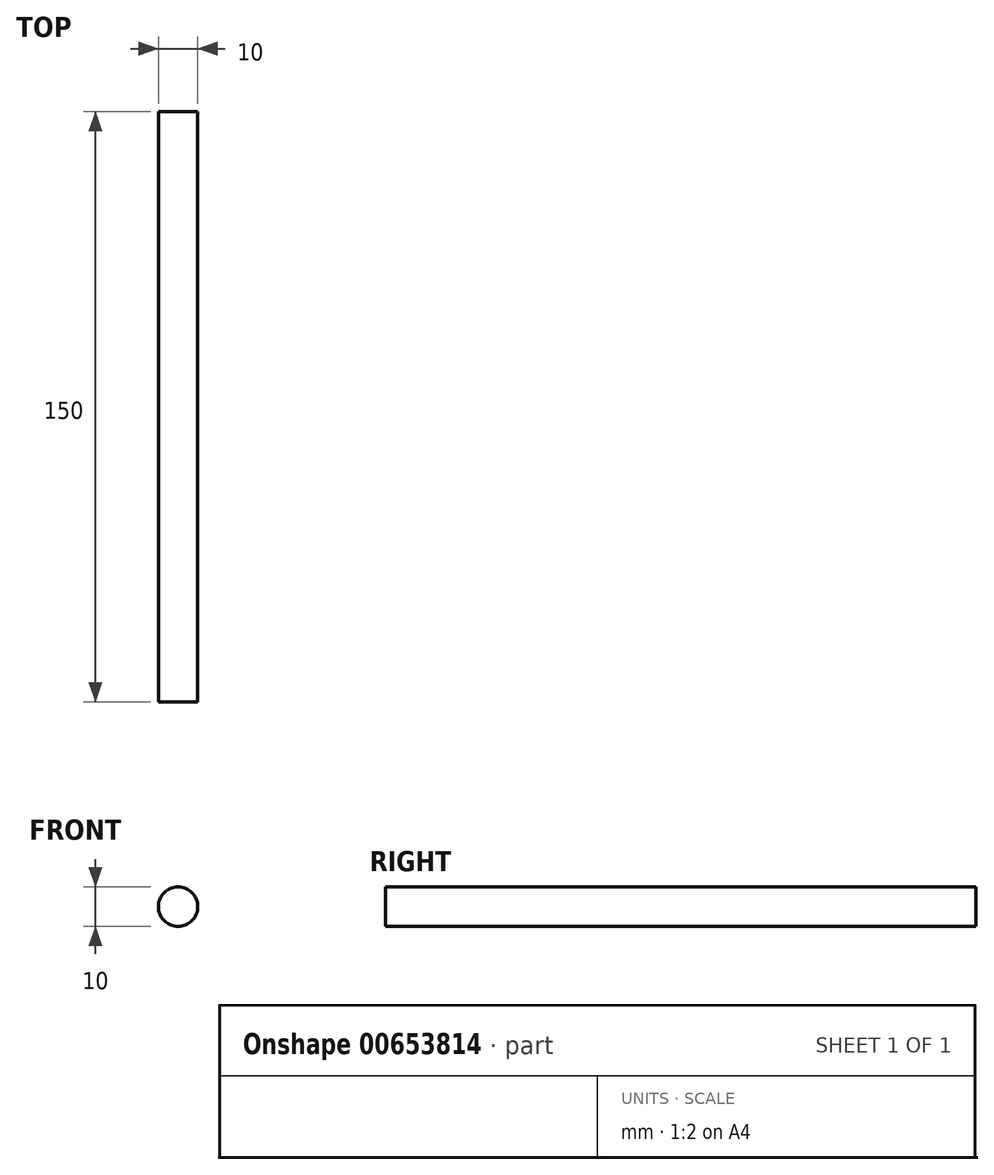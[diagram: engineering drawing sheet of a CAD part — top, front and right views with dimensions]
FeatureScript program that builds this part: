
annotation { "Feature Type Name" : "Feature", "Feature Type Description" : "" }
export const myFeature = defineFeature(function(context is Context, id is Id, definition is map)
    precondition{}
    {
        {
            var Q0;
            Q0=qCreatedBy(makeId("Right.planeOp"),FACE);
            var sketch = newSketch(context, id + "F0", { "sketchPlane" : qUnion([Q0])});
            skLineSegment(sketch, "E0", {"start": v(0, 0) * mm, "end": v(150, 0) * mm});
            skSolve(sketch);
        }
        {
            var Q0;
            Q0=qCreatedBy(makeId("Front.planeOp"),FACE);
            var sketch = newSketch(context, id + "F1", { "sketchPlane" : qUnion([Q0])});
            skCircle(sketch, "E1", {"center": v(0, 0) * mm, "radius": 5 * mm});
            skSolve(sketch);
        }
        {
            var Q0;
            Q0=makeQuery(id+"F1.imprint","IMPRINT",FACE,{"disambiguationData":[TD([[makeQuery(id+"F1.imprint","IMPRINT",EDGE,{"derivedFrom":sQuery(id+"F1.wireOp",EDGE,"E1")}),1.0]])]});
            var Q1;
            Q1=sQuery(id+"F0.wireOp",EDGE,"E0");
            sweep(context, id + "F2", {"profiles" : qUnion([Q0]), "path" : qUnion([Q1])});
        }
    });
